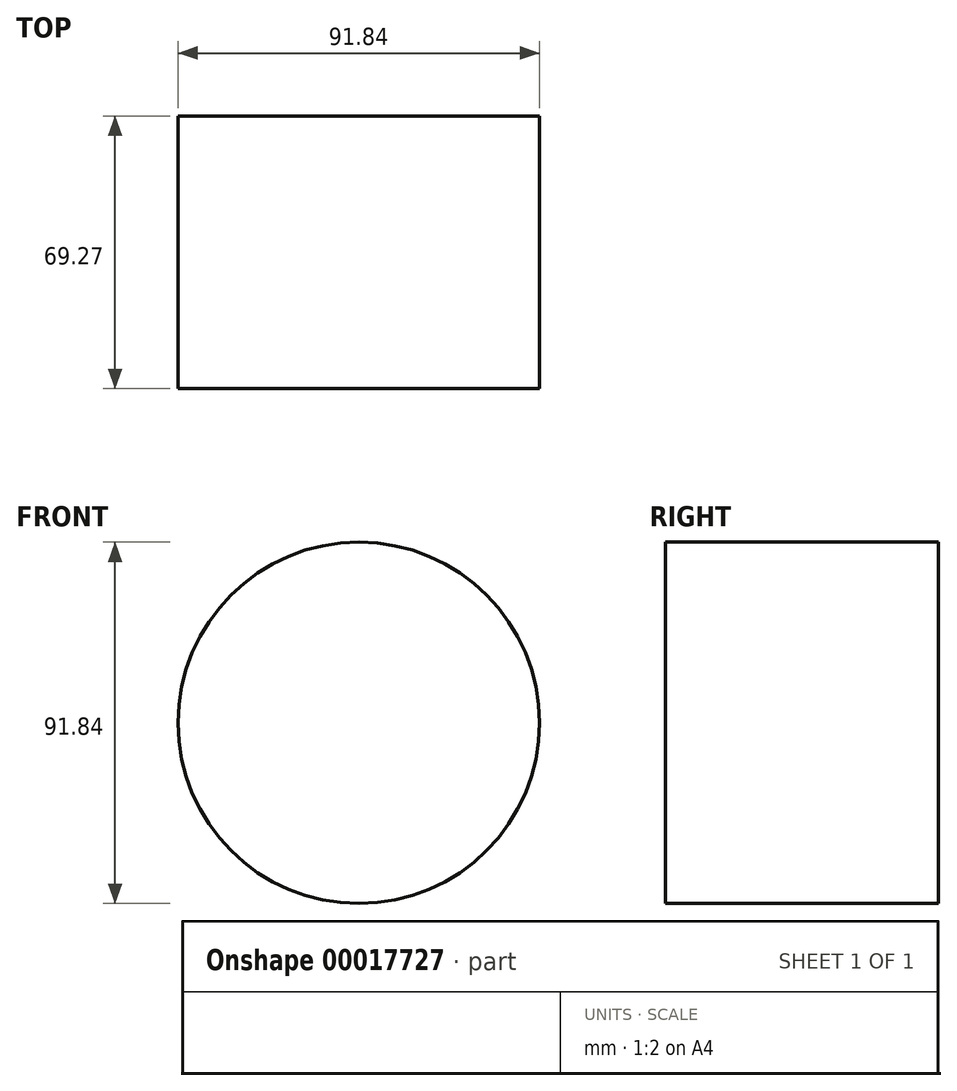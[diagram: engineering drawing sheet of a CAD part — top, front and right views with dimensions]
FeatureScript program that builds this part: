
annotation { "Feature Type Name" : "Feature", "Feature Type Description" : "" }
export const myFeature = defineFeature(function(context is Context, id is Id, definition is map)
    precondition{}
    {
        {
            var Q0;
            Q0=qCreatedBy(makeId("Front.planeOp"),FACE);
            var sketch = newSketch(context, id + "F2", { "sketchPlane" : qUnion([Q0])});
            skCircle(sketch, "E0", {"center": v(0, 0) * mm, "radius": 45.92 * mm});
            skSolve(sketch);
        }
        {
            var Q0;
            Q0=makeQuery(id+"F2.imprint","IMPRINT",FACE,{"disambiguationData":[TD([[makeQuery(id+"F2.imprint","IMPRINT",EDGE,{"derivedFrom":sQuery(id+"F2.wireOp",EDGE,"E0")}),1.0]])]});
            extrude(context, id + "F0", {"entities" : qUnion([Q0]), "depth" : 69.27 * mm});
        }
    });
